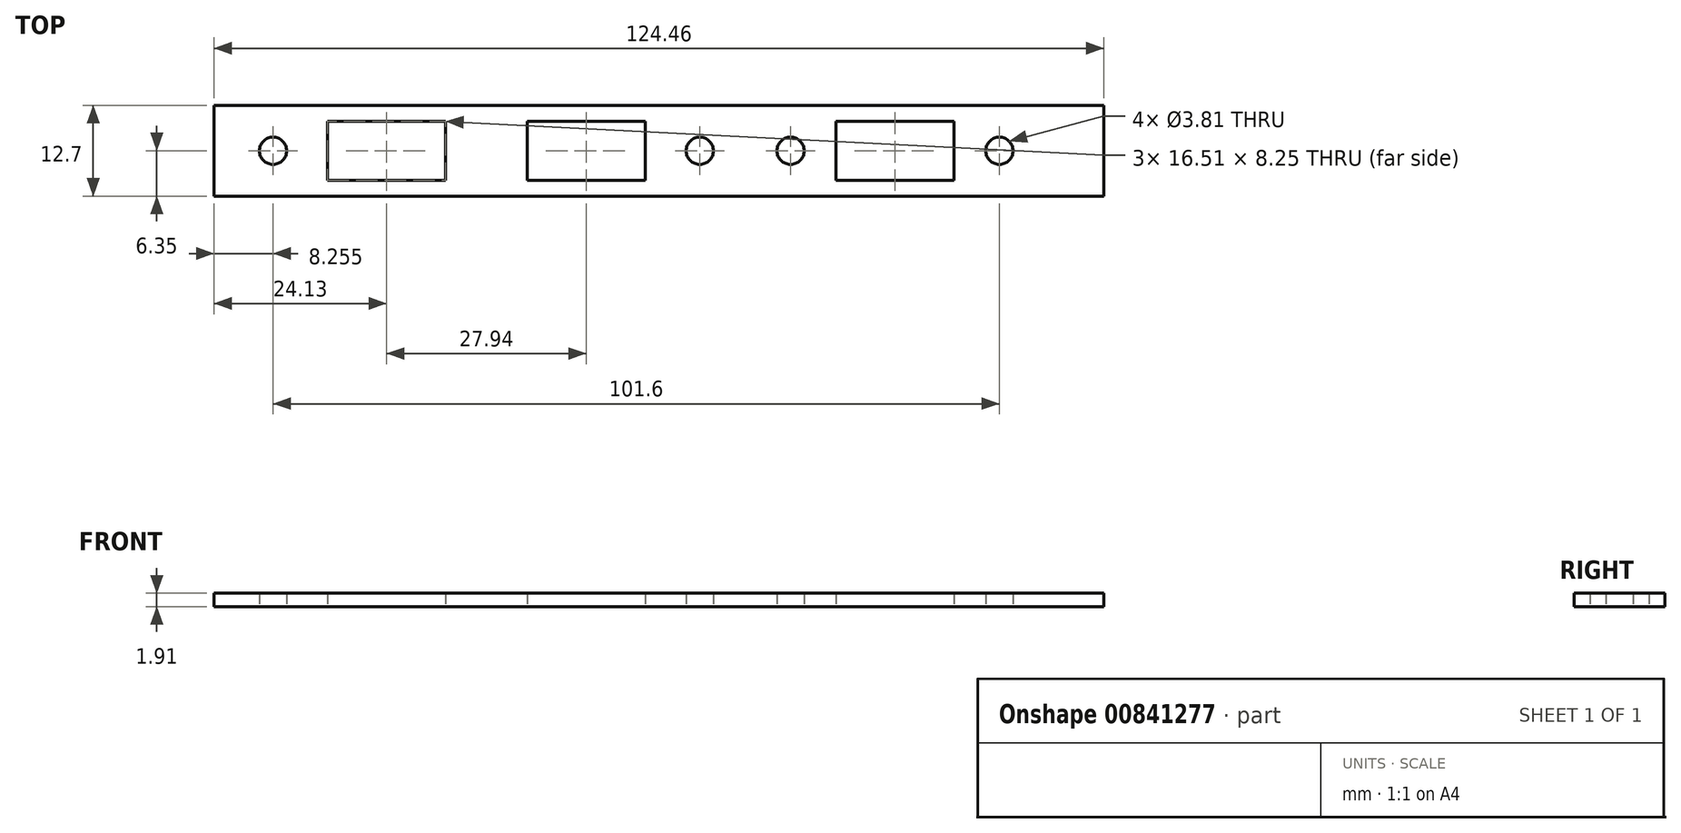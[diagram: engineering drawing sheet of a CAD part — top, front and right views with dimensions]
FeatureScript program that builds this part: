
annotation { "Feature Type Name" : "Feature", "Feature Type Description" : "" }
export const myFeature = defineFeature(function(context is Context, id is Id, definition is map)
    precondition{}
    {
        {
            var Q0;
            Q0=qCreatedBy(makeId("Top.planeOp"),FACE);
            var sketch = newSketch(context, id + "F0", { "sketchPlane" : qUnion([Q0])});
            skLineSegment(sketch, "E0.bottom", {"start": v(0, 0) * mm, "end": v(124.46, 0) * mm});
            skLineSegment(sketch, "E0.top", {"start": v(0, 12.7) * mm, "end": v(124.46, 12.7) * mm});
            skLineSegment(sketch, "E0.left", {"start": v(0, 0) * mm, "end": v(0, 12.7) * mm});
            skLineSegment(sketch, "E0.right", {"start": v(124.46, 0) * mm, "end": v(124.46, 12.7) * mm});
            skLineSegment(sketch, "E1", {"start": v(38.1, 12.7) * mm, "end": v(38.1, 0) * mm, "construction": true});
            skLineSegment(sketch, "E2.bottom", {"start": v(32.39, 10.48) * mm, "end": v(15.88, 10.48) * mm});
            skLineSegment(sketch, "E2.top", {"start": v(32.39, 2.22) * mm, "end": v(15.88, 2.22) * mm});
            skLineSegment(sketch, "E2.left", {"start": v(32.39, 10.48) * mm, "end": v(32.39, 2.22) * mm});
            skLineSegment(sketch, "E2.right", {"start": v(15.88, 10.48) * mm, "end": v(15.88, 2.22) * mm});
            skPoint(sketch, "E2.middle", {"position": v(24.13, 6.35) * mm});
            skPoint(sketch, "E3", {"position": v(38.1, 6.35) * mm});
            skCircle(sketch, "E4", {"center": v(8.25, 6.35) * mm, "radius": 1.9 * mm});
            skPoint(sketch, "E4.centerSnap0", {"position": v(15.88, 6.35) * mm});
            skLineSegment(sketch, "E5.MirrorCS", {"start": v(43.82, 10.48) * mm, "end": v(43.82, 2.22) * mm});
            skLineSegment(sketch, "E6.MirrorCS", {"start": v(43.82, 10.48) * mm, "end": v(60.33, 10.48) * mm});
            skLineSegment(sketch, "E7.MirrorCS", {"start": v(60.33, 10.48) * mm, "end": v(60.33, 2.22) * mm});
            skPoint(sketch, "E8.MirrorP", {"position": v(60.33, 6.35) * mm});
            skCircle(sketch, "E9.MirrorC", {"center": v(67.95, 6.35) * mm, "radius": 1.9 * mm});
            skPoint(sketch, "E10.MirrorP", {"position": v(52.07, 6.35) * mm});
            skLineSegment(sketch, "E11.MirrorCS", {"start": v(43.82, 2.22) * mm, "end": v(60.33, 2.22) * mm});
            skLineSegment(sketch, "E12", {"start": v(95.25, 12.7) * mm, "end": v(95.25, 0) * mm, "construction": true});
            skLineSegment(sketch, "E13.bottom", {"start": v(103.5, 10.48) * mm, "end": v(87, 10.48) * mm});
            skLineSegment(sketch, "E13.top", {"start": v(103.5, 2.22) * mm, "end": v(87, 2.22) * mm});
            skLineSegment(sketch, "E13.left", {"start": v(103.5, 10.48) * mm, "end": v(103.5, 2.22) * mm});
            skLineSegment(sketch, "E13.right", {"start": v(87, 10.48) * mm, "end": v(87, 2.22) * mm});
            skPoint(sketch, "E13.middle", {"position": v(95.25, 6.35) * mm});
            skCircle(sketch, "E14", {"center": v(80.65, 6.35) * mm, "radius": 1.9 * mm});
            skCircle(sketch, "E15.MirrorC", {"center": v(109.86, 6.35) * mm, "radius": 1.9 * mm});
            skSolve(sketch);
        }
        {
            var Q0;
            Q0=makeQuery(id+"F0.imprint","IMPRINT",FACE,{"disambiguationData":[TD([[makeQuery(id+"F0.imprint","IMPRINT",EDGE,{"derivedFrom":sQuery(id+"F0.wireOp",EDGE,"E0.bottom")}),1.0]])]});
            extrude(context, id + "F1", {"entities" : qUnion([Q0]), "depth" : 1.9 * mm, "offsetDistance" : 25.4 * mm});
        }
    });
